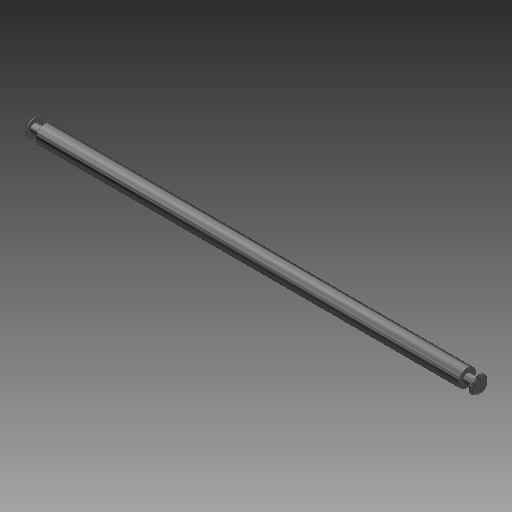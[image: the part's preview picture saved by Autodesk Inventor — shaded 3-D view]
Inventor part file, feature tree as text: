
AUTODESK INVENTOR PART (.ipt)
format: ipt  version: 2019 (Build 230136000, 136)  size: 123,904 bytes
history: native  units: mm
features: revolve x1, chamfer x1, fillet x1, sketch x1
ambient origin geometry x8: Origin, YZ Plane, XZ Plane, XY Plane, X Axis, Y Axis, Z Axis, Center Point
bodies: Solid1 (feature_tree)
feature tree (4):
  revolve  "Revolution1"  [1 undecoded]
  chamfer  "Chamfer1"  Distance=8.36mm
  fillet  "Fillet1"  Radius=15.84mm
  sketch  "Sketch1"  dims[d0=400.5mm d2=15.84mm d4=8.36mm d5=15.84mm d7=8.36mm d8=15.84mm d15=2.875mm d16=90.0deg d17=0.375mm d18=2.0mm d19=45.0deg d20=0.5mm d21=2.95mm d22=8.8mm d23=2.95mm d24=8.8mm]
note: 1 required parameter value undecoded (feature->parameter linkage not recoverable at this tier; creation-order binding heuristic only, values carry confidence <= 0.55)
